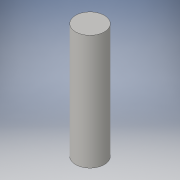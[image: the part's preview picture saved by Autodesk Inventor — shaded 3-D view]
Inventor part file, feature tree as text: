
AUTODESK INVENTOR PART (.ipt)
format: ipt  version: 2016 (Build 200138000, 138)  size: 84,992 bytes
history: native  units: in
note: dims shown in document units (in); Inventor stores cm internally (conversion verified against a paired STEP export)
features: extrude x1, sketch x1
ambient origin geometry x8: Origin, YZ Plane, XZ Plane, XY Plane, X Axis, Y Axis, Z Axis, Center Point
bodies: Solid1 (feature_tree)
feature tree (2):
  extrude  "Extrusion1"  Depth=1.5748in TaperAngle=0.0deg
  sketch  "Sketch1"  dims[d0=0.3937in d1=1.5748in d2=0.0in]
